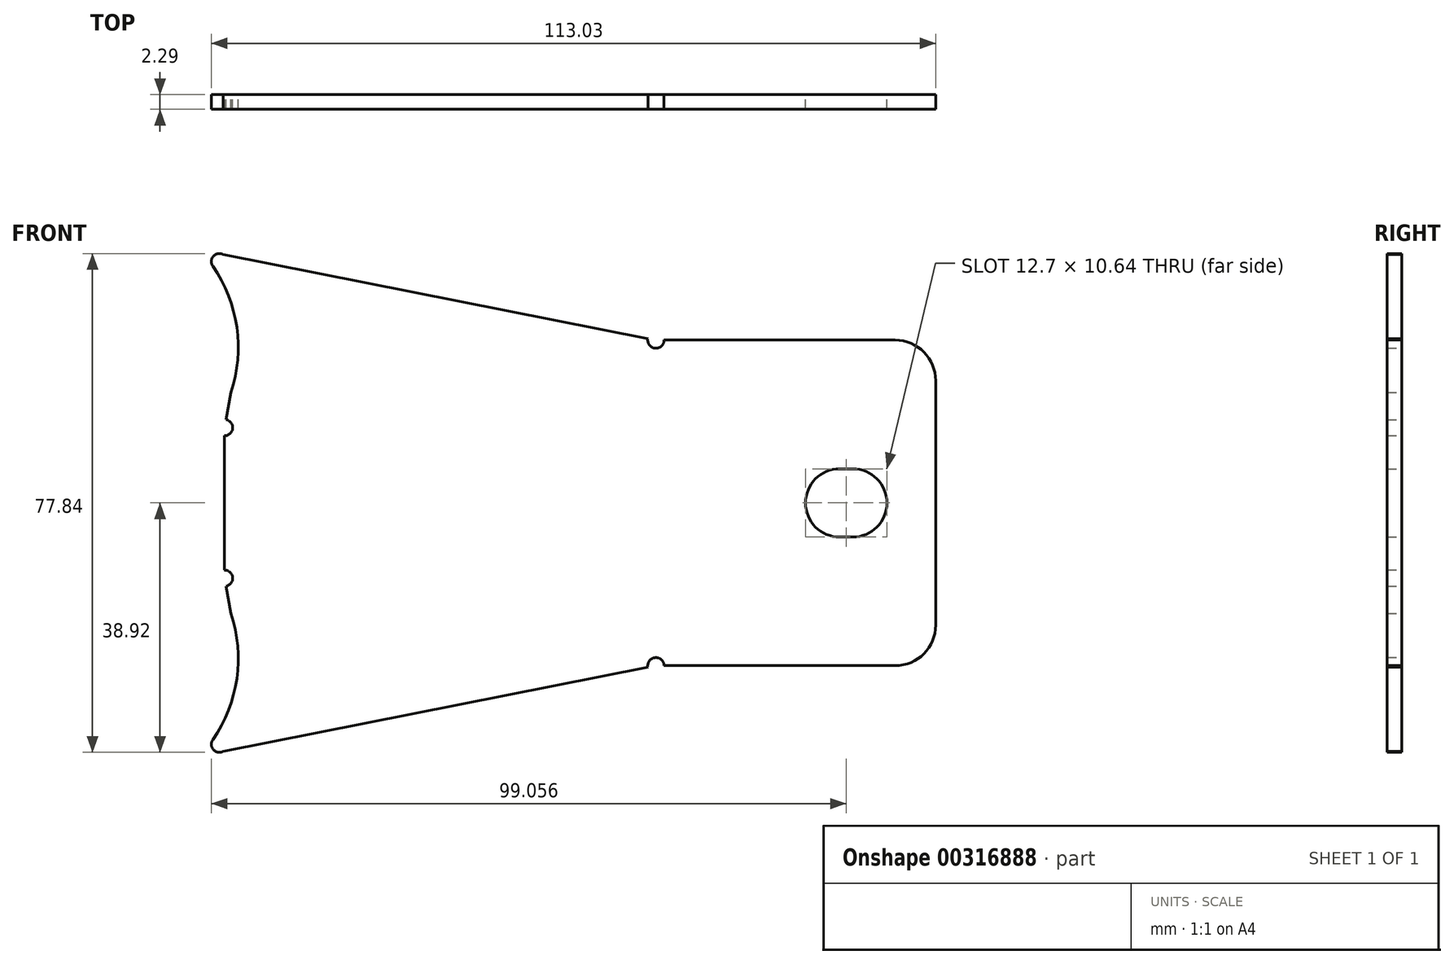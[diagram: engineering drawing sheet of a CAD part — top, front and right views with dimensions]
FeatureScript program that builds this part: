
annotation { "Feature Type Name" : "Feature", "Feature Type Description" : "" }
export const myFeature = defineFeature(function(context is Context, id is Id, definition is map)
    precondition{}
    {
        {
            var Q0;
            Q0=qCreatedBy(makeId("Front.planeOp"),FACE);
            var sketch = newSketch(context, id + "F0", { "sketchPlane" : qUnion([Q0])});
            skArc(sketch, "E0", {"start": v(-23.03, -36.92) * mm, "mid": v(-22.93, -38.5) * mm, "end": v(-21.38, -38.76) * mm});
            skArc(sketch, "E1", {"start": v(-23.03, -36.92) * mm, "mid": v(-19.28, -27.42) * mm, "end": v(-20.18, -17.25) * mm});
            skLineSegment(sketch, "E2", {"start": v(-20.97, -13) * mm, "end": v(-20.18, -17.25) * mm});
            skLineSegment(sketch, "E3", {"start": v(-21.2, 10.48) * mm, "end": v(-21.2, -10.48) * mm});
            skLineSegment(sketch, "E4", {"start": v(-20.18, 17.25) * mm, "end": v(-20.97, 13) * mm});
            skArc(sketch, "E5", {"start": v(-20.18, 17.25) * mm, "mid": v(-19.28, 27.42) * mm, "end": v(-23.03, 36.92) * mm});
            skArc(sketch, "E6", {"start": v(-21.38, 38.76) * mm, "mid": v(-22.93, 38.5) * mm, "end": v(-23.03, 36.92) * mm});
            skArc(sketch, "E7", {"start": v(76.83, 5.32) * mm, "mid": v(82.16, 0) * mm, "end": v(76.83, -5.32) * mm});
            skLineSegment(sketch, "E8", {"start": v(89.78, 19.05) * mm, "end": v(89.78, -19.05) * mm});
            skArc(sketch, "E9", {"start": v(74.78, 5.32) * mm, "mid": v(69.46, 0) * mm, "end": v(74.78, -5.32) * mm});
            skLineSegment(sketch, "E10", {"start": v(74.78, 5.32) * mm, "end": v(76.83, 5.32) * mm});
            skLineSegment(sketch, "E11", {"start": v(74.78, -5.32) * mm, "end": v(76.83, -5.32) * mm});
            skLineSegment(sketch, "E12", {"start": v(-21.38, 38.76) * mm, "end": v(44.87, 25.65) * mm});
            skLineSegment(sketch, "E13", {"start": v(-21.38, -38.76) * mm, "end": v(44.87, -25.65) * mm});
            skLineSegment(sketch, "E14", {"start": v(47.38, 25.4) * mm, "end": v(83.43, 25.4) * mm});
            skLineSegment(sketch, "E15", {"start": v(47.38, -25.4) * mm, "end": v(83.43, -25.4) * mm});
            skPoint(sketch, "E16.visualSharp", {"position": v(89.78, 25.4) * mm});
            skArc(sketch, "E16.filletArc", {"start": v(89.78, 19.05) * mm, "mid": v(87.92, 23.54) * mm, "end": v(83.43, 25.4) * mm});
            skPoint(sketch, "E17.visualSharp", {"position": v(89.78, -25.4) * mm});
            skArc(sketch, "E17.filletArc", {"start": v(83.43, -25.4) * mm, "mid": v(87.92, -23.54) * mm, "end": v(89.78, -19.05) * mm});
            skArc(sketch, "E18", {"start": v(-20.97, -13) * mm, "mid": v(-19.93, -11.63) * mm, "end": v(-21.2, -10.48) * mm});
            skArc(sketch, "E19", {"start": v(-21.2, 10.48) * mm, "mid": v(-19.93, 11.63) * mm, "end": v(-20.97, 13) * mm});
            skArc(sketch, "E20", {"start": v(44.87, 25.65) * mm, "mid": v(45.99, 24.14) * mm, "end": v(47.38, 25.4) * mm});
            skArc(sketch, "E21", {"start": v(47.38, -25.4) * mm, "mid": v(45.99, -24.14) * mm, "end": v(44.87, -25.65) * mm});
            skPoint(sketch, "E22.orphan", {"position": v(46.11, 0) * mm});
            skLineSegment(sketch, "E23", {"start": v(47.38, 25.4) * mm, "end": v(76.83, 5.32) * mm});
            skLineSegment(sketch, "E24", {"start": v(76.83, -5.32) * mm, "end": v(47.38, -25.4) * mm});
            skSolve(sketch);
        }
        {
            var Q0;
            Q0 = qSketchRegion(id + "F0", true);
            extrude(context, id + "F1", {"entities" : qUnion([Q0]), "depth" : 2.3 * mm});
        }
    });
